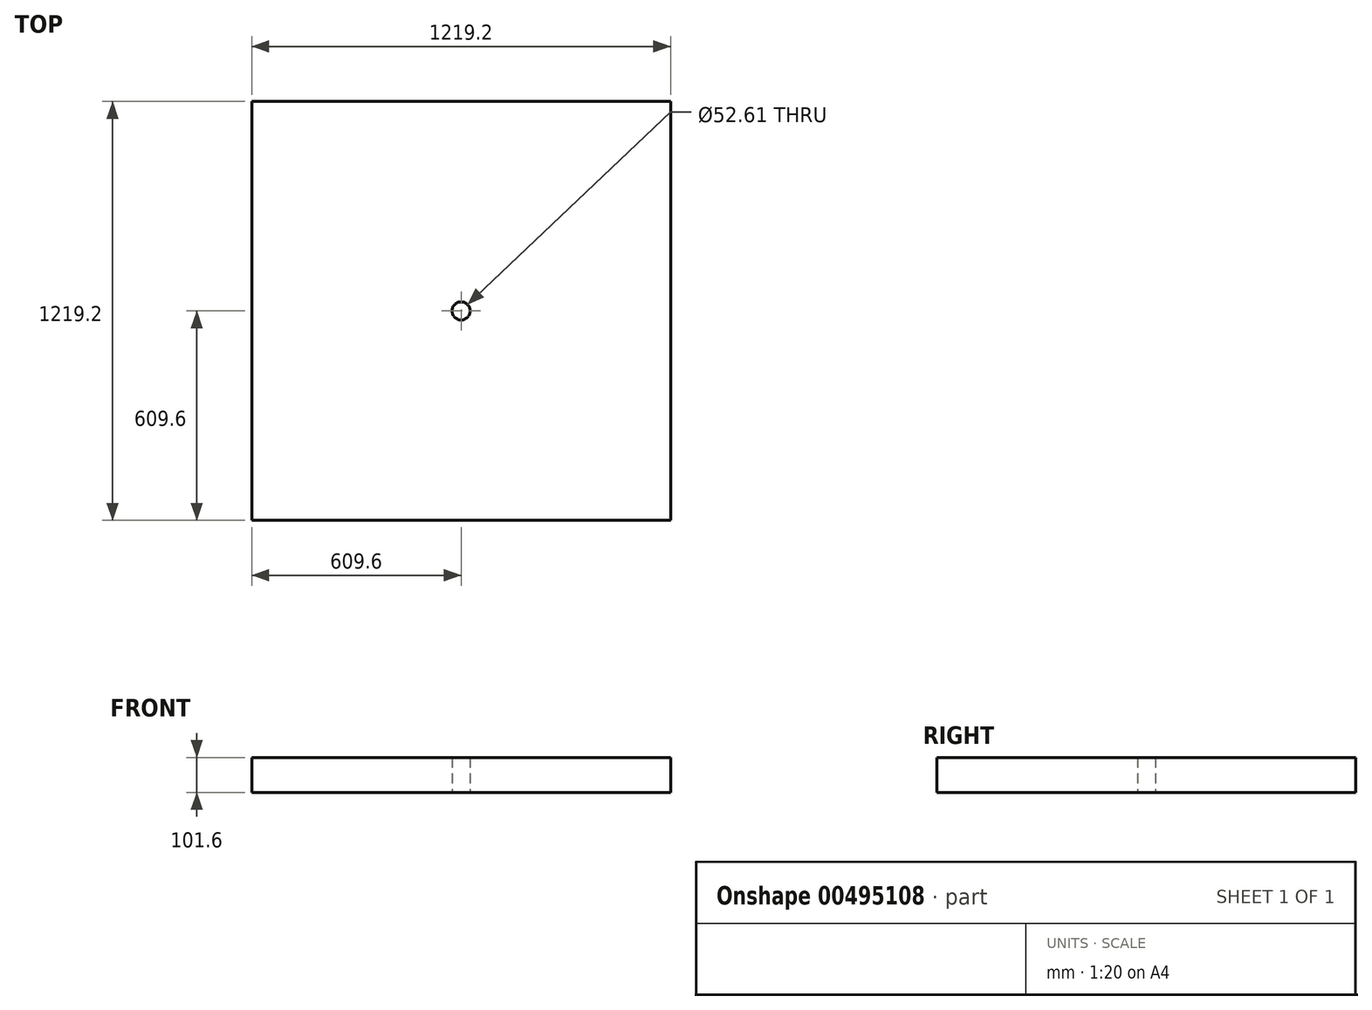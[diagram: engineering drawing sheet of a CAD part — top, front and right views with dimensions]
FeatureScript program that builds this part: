
annotation { "Feature Type Name" : "Feature", "Feature Type Description" : "" }
export const myFeature = defineFeature(function(context is Context, id is Id, definition is map)
    precondition{}
    {
        {
            var Q0;
            Q0=qCreatedBy(makeId("Top.planeOp"),FACE);
            var sketch = newSketch(context, id + "F0", { "sketchPlane" : qUnion([Q0])});
            skLineSegment(sketch, "E0", {"start": v(609.6, 609.6) * mm, "end": v(-609.6, 609.6) * mm});
            skLineSegment(sketch, "E1", {"start": v(-609.6, 609.6) * mm, "end": v(-609.6, -609.6) * mm});
            skLineSegment(sketch, "E2", {"start": v(-609.6, -609.6) * mm, "end": v(609.6, -609.6) * mm});
            skLineSegment(sketch, "E3", {"start": v(609.6, -609.6) * mm, "end": v(609.6, 609.6) * mm});
            skCircle(sketch, "E4", {"center": v(0, 0) * mm, "radius": 26.3 * mm});
            skCircle(sketch, "E5", {"center": v(0, 0) * mm, "radius": 25.4 * mm});
            skSolve(sketch);
        }
        {
            var Q0;
            Q0=makeQuery(id+"F0.imprint","IMPRINT",FACE,{"disambiguationData":[TD([[makeQuery(id+"F0.imprint","IMPRINT",EDGE,{"derivedFrom":sQuery(id+"F0.wireOp",EDGE,"E0")}),1.0]])]});
            extrude(context, id + "F1", {"entities" : qUnion([Q0]), "depth" : 101.6 * mm});
        }
    });
